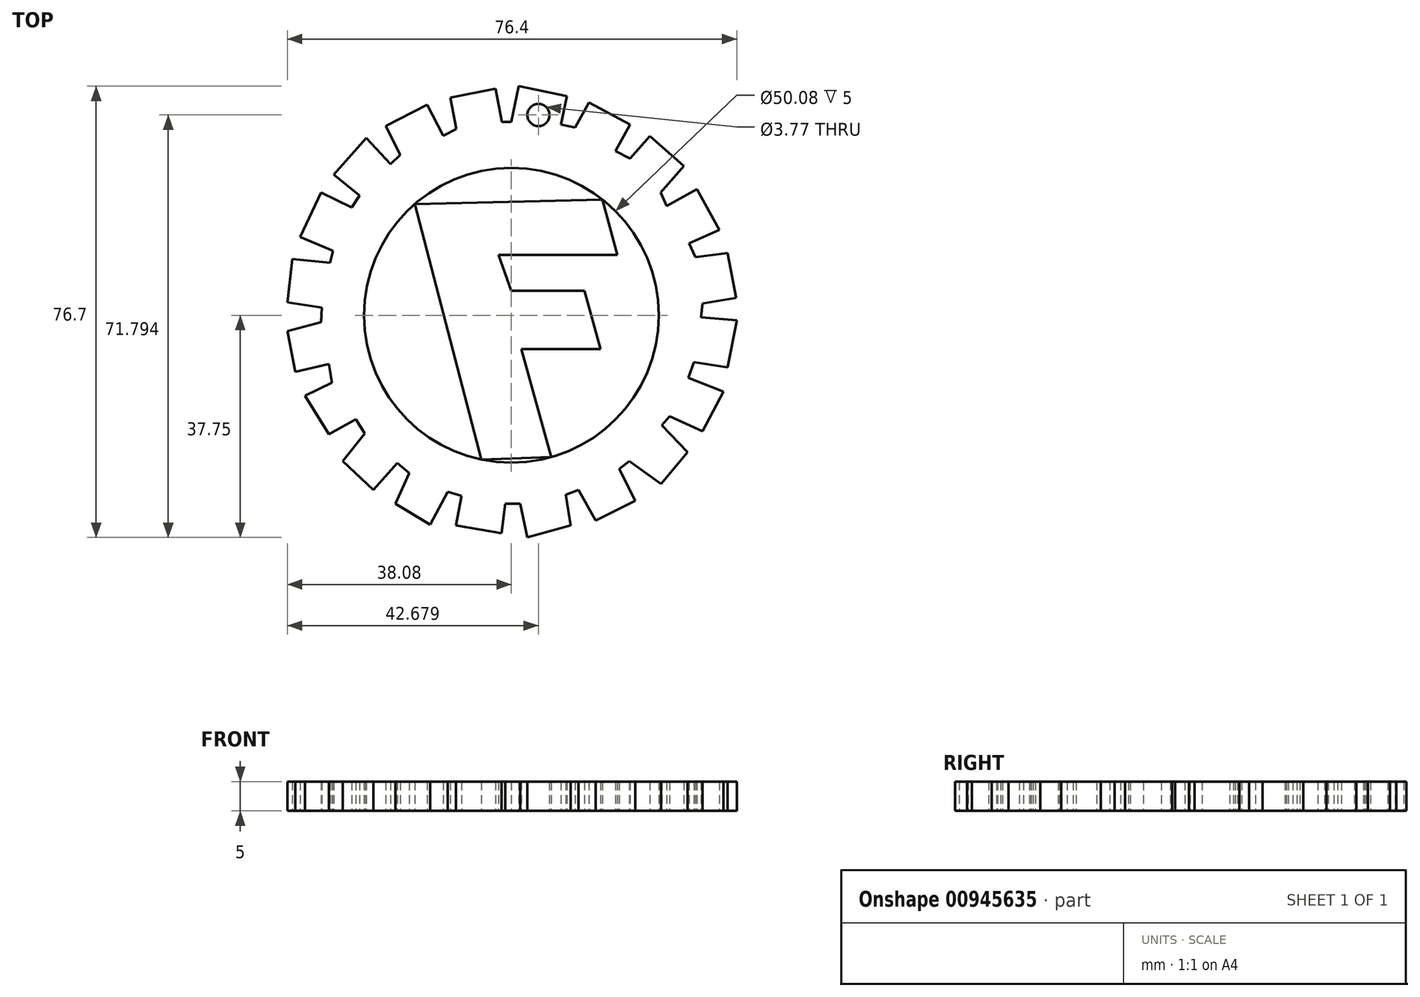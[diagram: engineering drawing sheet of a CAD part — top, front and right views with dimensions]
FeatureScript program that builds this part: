
annotation { "Feature Type Name" : "Feature", "Feature Type Description" : "" }
export const myFeature = defineFeature(function(context is Context, id is Id, definition is map)
    precondition{}
    {
        {
            var Q0;
            Q0=qCreatedBy(makeId("Top.planeOp"),FACE);
            var sketch = newSketch(context, id + "F0", { "sketchPlane" : qUnion([Q0])});
            skLineSegment(sketch, "E0", {"start": v(-24.69, 30.12) * mm, "end": v(-20.52, 25.71) * mm});
            skLineSegment(sketch, "E1", {"start": v(-20.52, 25.71) * mm, "end": v(-18.86, 27.28) * mm});
            skLineSegment(sketch, "E2", {"start": v(-18.86, 27.28) * mm, "end": v(-21.35, 32.14) * mm});
            skLineSegment(sketch, "E3", {"start": v(-21.35, 32.14) * mm, "end": v(-14.29, 35.77) * mm});
            skLineSegment(sketch, "E4", {"start": v(-14.29, 35.77) * mm, "end": v(-11.6, 30.52) * mm});
            skLineSegment(sketch, "E5", {"start": v(-11.6, 30.52) * mm, "end": v(-9.38, 31.66) * mm});
            skLineSegment(sketch, "E6", {"start": v(-9.38, 31.66) * mm, "end": v(-10.4, 37.03) * mm});
            skLineSegment(sketch, "E7", {"start": v(-10.4, 37.03) * mm, "end": v(-2.65, 38.5) * mm});
            skLineSegment(sketch, "E8", {"start": v(-2.65, 38.5) * mm, "end": v(-1.6, 32.88) * mm});
            skLineSegment(sketch, "E9", {"start": v(-1.6, 32.88) * mm, "end": v(0, 32.88) * mm});
            skLineSegment(sketch, "E10", {"start": v(0, 32.88) * mm, "end": v(1.28, 38.95) * mm});
            skLineSegment(sketch, "E11", {"start": v(1.28, 38.95) * mm, "end": v(9.44, 37.23) * mm});
            skLineSegment(sketch, "E12", {"start": v(9.44, 37.23) * mm, "end": v(8.43, 32.4) * mm});
            skLineSegment(sketch, "E13", {"start": v(8.43, 32.4) * mm, "end": v(10.86, 31.9) * mm});
            skLineSegment(sketch, "E14", {"start": v(10.86, 31.9) * mm, "end": v(13.19, 36.2) * mm});
            skLineSegment(sketch, "E15", {"start": v(13.19, 36.2) * mm, "end": v(20.16, 32.42) * mm});
            skLineSegment(sketch, "E16", {"start": v(20.16, 32.42) * mm, "end": v(17.73, 27.93) * mm});
            skLineSegment(sketch, "E17", {"start": v(17.73, 27.93) * mm, "end": v(20.15, 26.62) * mm});
            skLineSegment(sketch, "E18", {"start": v(20.15, 26.62) * mm, "end": v(23.55, 30.48) * mm});
            skLineSegment(sketch, "E19", {"start": v(23.55, 30.48) * mm, "end": v(29.35, 25.37) * mm});
            skLineSegment(sketch, "E20", {"start": v(29.35, 25.37) * mm, "end": v(25.39, 20.87) * mm});
            skLineSegment(sketch, "E21", {"start": v(25.39, 20.87) * mm, "end": v(26.4, 18.57) * mm});
            skLineSegment(sketch, "E22", {"start": v(26.4, 18.57) * mm, "end": v(31.53, 21.42) * mm});
            skLineSegment(sketch, "E23", {"start": v(31.53, 21.42) * mm, "end": v(35.37, 14.54) * mm});
            skLineSegment(sketch, "E24", {"start": v(35.37, 14.54) * mm, "end": v(30.22, 12.25) * mm});
            skLineSegment(sketch, "E25", {"start": v(30.22, 12.25) * mm, "end": v(31.3, 9.87) * mm});
            skLineSegment(sketch, "E26", {"start": v(31.3, 9.87) * mm, "end": v(36.77, 10.59) * mm});
            skLineSegment(sketch, "E27", {"start": v(36.77, 10.59) * mm, "end": v(38.2, 2.96) * mm});
            skLineSegment(sketch, "E28", {"start": v(38.2, 2.96) * mm, "end": v(32.48, 2.01) * mm});
            skLineSegment(sketch, "E29", {"start": v(32.48, 2.01) * mm, "end": v(32.24, -0.37) * mm});
            skLineSegment(sketch, "E30", {"start": v(32.24, -0.37) * mm, "end": v(38.32, -0.85) * mm});
            skLineSegment(sketch, "E31", {"start": v(38.32, -0.85) * mm, "end": v(36.77, -8.83) * mm});
            skLineSegment(sketch, "E32", {"start": v(36.77, -8.83) * mm, "end": v(31.05, -8) * mm});
            skLineSegment(sketch, "E33", {"start": v(31.05, -8) * mm, "end": v(30.1, -10.61) * mm});
            skLineSegment(sketch, "E34", {"start": v(30.1, -10.61) * mm, "end": v(36.05, -13) * mm});
            skLineSegment(sketch, "E35", {"start": v(36.05, -13) * mm, "end": v(32.5, -19.73) * mm});
            skLineSegment(sketch, "E36", {"start": v(32.5, -19.73) * mm, "end": v(26.94, -17.2) * mm});
            skLineSegment(sketch, "E37", {"start": v(26.94, -17.2) * mm, "end": v(25.59, -18.72) * mm});
            skLineSegment(sketch, "E38", {"start": v(25.59, -18.72) * mm, "end": v(29.97, -23.26) * mm});
            skLineSegment(sketch, "E39", {"start": v(29.97, -23.26) * mm, "end": v(25.42, -28.65) * mm});
            skLineSegment(sketch, "E40", {"start": v(25.42, -28.65) * mm, "end": v(20.03, -24.78) * mm});
            skLineSegment(sketch, "E41", {"start": v(20.03, -24.78) * mm, "end": v(18.35, -26.13) * mm});
            skLineSegment(sketch, "E42", {"start": v(18.35, -26.13) * mm, "end": v(21.04, -31.52) * mm});
            skLineSegment(sketch, "E43", {"start": v(21.04, -31.52) * mm, "end": v(14.3, -34.89) * mm});
            skLineSegment(sketch, "E44", {"start": v(14.3, -34.89) * mm, "end": v(11.44, -29.66) * mm});
            skLineSegment(sketch, "E45", {"start": v(11.44, -29.66) * mm, "end": v(9.25, -30.5) * mm});
            skLineSegment(sketch, "E46", {"start": v(9.25, -30.5) * mm, "end": v(10.1, -35.73) * mm});
            skLineSegment(sketch, "E47", {"start": v(10.1, -35.73) * mm, "end": v(2.68, -37.75) * mm});
            skLineSegment(sketch, "E48", {"start": v(2.68, -37.75) * mm, "end": v(1.5, -32.02) * mm});
            skLineSegment(sketch, "E49", {"start": v(1.5, -32.02) * mm, "end": v(-1.02, -32.02) * mm});
            skLineSegment(sketch, "E50", {"start": v(-1.02, -32.02) * mm, "end": v(-1.7, -37.07) * mm});
            skLineSegment(sketch, "E51", {"start": v(-1.7, -37.07) * mm, "end": v(-9.45, -35.73) * mm});
            skLineSegment(sketch, "E52", {"start": v(-9.45, -35.73) * mm, "end": v(-8.44, -30.67) * mm});
            skLineSegment(sketch, "E53", {"start": v(-8.44, -30.67) * mm, "end": v(-10.8, -30) * mm});
            skLineSegment(sketch, "E54", {"start": v(-10.8, -30) * mm, "end": v(-13.83, -35.56) * mm});
            skLineSegment(sketch, "E55", {"start": v(-13.83, -35.56) * mm, "end": v(-19.72, -32.02) * mm});
            skLineSegment(sketch, "E56", {"start": v(-19.72, -32.02) * mm, "end": v(-17.36, -26.8) * mm});
            skLineSegment(sketch, "E57", {"start": v(-17.36, -26.8) * mm, "end": v(-19.38, -25.12) * mm});
            skLineSegment(sketch, "E58", {"start": v(-19.38, -25.12) * mm, "end": v(-23.43, -29.66) * mm});
            skLineSegment(sketch, "E59", {"start": v(-23.43, -29.66) * mm, "end": v(-28.65, -24.78) * mm});
            skLineSegment(sketch, "E60", {"start": v(-28.65, -24.78) * mm, "end": v(-24.94, -20.06) * mm});
            skLineSegment(sketch, "E61", {"start": v(-24.94, -20.06) * mm, "end": v(-26.46, -17.7) * mm});
            skLineSegment(sketch, "E62", {"start": v(-26.46, -17.7) * mm, "end": v(-31, -20.23) * mm});
            skLineSegment(sketch, "E63", {"start": v(-31, -20.23) * mm, "end": v(-35.05, -13.66) * mm});
            skLineSegment(sketch, "E64", {"start": v(-35.05, -13.66) * mm, "end": v(-30.5, -11.47) * mm});
            skLineSegment(sketch, "E65", {"start": v(-30.5, -11.47) * mm, "end": v(-31, -8.27) * mm});
            skLineSegment(sketch, "E66", {"start": v(-31, -8.27) * mm, "end": v(-36.73, -9.62) * mm});
            skLineSegment(sketch, "E67", {"start": v(-36.73, -9.62) * mm, "end": v(-38.08, -2.71) * mm});
            skLineSegment(sketch, "E68", {"start": v(-38.08, -2.71) * mm, "end": v(-32.35, -1.2) * mm});
            skLineSegment(sketch, "E69", {"start": v(-32.35, -1.2) * mm, "end": v(-32.18, 1.33) * mm});
            skLineSegment(sketch, "E70", {"start": v(-32.18, 1.33) * mm, "end": v(-38.08, 2.17) * mm});
            skLineSegment(sketch, "E71", {"start": v(-38.08, 2.17) * mm, "end": v(-37.24, 9.58) * mm});
            skLineSegment(sketch, "E72", {"start": v(-37.24, 9.58) * mm, "end": v(-30.84, 8.9) * mm});
            skLineSegment(sketch, "E73", {"start": v(-30.84, 8.9) * mm, "end": v(-30.33, 10.93) * mm});
            skLineSegment(sketch, "E74", {"start": v(-30.33, 10.93) * mm, "end": v(-35.9, 13.29) * mm});
            skLineSegment(sketch, "E75", {"start": v(-35.9, 13.29) * mm, "end": v(-32.35, 20.87) * mm});
            skLineSegment(sketch, "E76", {"start": v(-32.35, 20.87) * mm, "end": v(-27.13, 18.34) * mm});
            skLineSegment(sketch, "E77", {"start": v(-27.13, 18.34) * mm, "end": v(-25.78, 20.36) * mm});
            skLineSegment(sketch, "E78", {"start": v(-25.78, 20.36) * mm, "end": v(-30.16, 23.9) * mm});
            skLineSegment(sketch, "E79", {"start": v(-24.69, 30.12) * mm, "end": v(-30.16, 23.9) * mm});
            skCircle(sketch, "E80", {"center": v(0, 0) * mm, "radius": 25.04 * mm});
            skLineSegment(sketch, "E81", {"start": v(-16.41, 18.91) * mm, "end": v(-5.12, -24.5) * mm});
            skLineSegment(sketch, "E82", {"start": v(-5.12, -24.5) * mm, "end": v(6.78, -24.1) * mm});
            skLineSegment(sketch, "E83", {"start": v(6.78, -24.1) * mm, "end": v(1.67, -5.75) * mm});
            skLineSegment(sketch, "E84", {"start": v(1.67, -5.75) * mm, "end": v(15.15, -5.75) * mm});
            skLineSegment(sketch, "E85", {"start": v(15.15, -5.75) * mm, "end": v(12.45, 4.2) * mm});
            skLineSegment(sketch, "E86", {"start": v(12.45, 4.2) * mm, "end": v(0, 4.2) * mm});
            skLineSegment(sketch, "E87", {"start": v(0, 4.2) * mm, "end": v(-2.2, 10.26) * mm});
            skLineSegment(sketch, "E88", {"start": v(-2.2, 10.26) * mm, "end": v(18, 10.26) * mm});
            skLineSegment(sketch, "E89", {"start": v(18, 10.26) * mm, "end": v(15.48, 19.68) * mm});
            skLineSegment(sketch, "E90", {"start": v(15.48, 19.68) * mm, "end": v(-16.41, 18.91) * mm});
            skCircle(sketch, "E91", {"center": v(4.6, 34.04) * mm, "radius": 1.88 * mm});
            skPoint(sketch, "E91.centerSnap0", {"position": v(12.02, 34.04) * mm});
            skSolve(sketch);
        }
        {
            var Q0;
            Q0 = qSketchRegion(id + "F0", true);
            var Q1;
            Q1=makeQuery(id+"F0.imprint","IMPRINT",FACE,{"disambiguationData":[TD([[makeQuery(id+"F0.imprint","IMPRINT",EDGE,{"derivedFrom":sQuery(id+"F0.wireOp",EDGE,"E81")}),1.0]])]});
            extrude(context, id + "F1", {"entities" : qUnion([Q0, Q1]), "depth" : 5 * mm, "offsetDistance" : 25 * mm});
        }
    });
